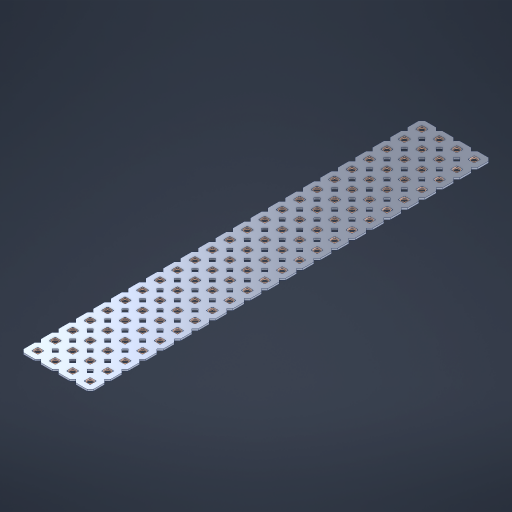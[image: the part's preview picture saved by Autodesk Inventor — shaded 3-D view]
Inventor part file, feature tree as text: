
AUTODESK INVENTOR PART (.ipt)
format: ipt  version: 2023 (Build 270158000, 158)  size: 1,322,496 bytes
history: native  units: in
note: dims shown in document units (in); Inventor stores cm internally (conversion verified against a paired STEP export)
features: other x93, extrude x91, sketch x2, pattern_linear x1
ambient origin geometry x8: Origin, YZ Plane, XZ Plane, XY Plane, X Axis, Y Axis, Z Axis, Center Point
bodies: Solid1 (feature_tree), Body (feature_tree)
feature tree (187):
  pattern_linear  "Rectangular Pattern1"  Spacing1=0.09in  [1 undecoded]
  sketch  "Sketch1"  dims[d1=0.5in]
  sketch  "Sketch2"  dims[d2=0.182in d3=0.09in d4=0.09in d5=0.09in d6=0.09in d7=0.09in d8=0.09in d9=0.09in d10=0.09in d11=0.02in d13=0.0in d14=0.172in d15=0.0625in d16=0.0in d19=0.5in d22=0.5in]
  other  "Srf1"
  other  "Srf126"
  other  "Srf127"
  other  "Srf128"
  other  "Srf129"
  other  "Srf130"
  other  "Srf131"
  other  "Srf250"
  other  "Srf251"
  other  "Srf252"
  other  "Srf253"
  other  "Srf254"
  other  "Srf255"
  other  "Srf256"
  other  "Srf257"
  other  "Srf258"
  other  "Srf259"
  other  "Srf260"
  other  "Srf261"
  other  "Srf262"
  other  "Srf263"
  other  "Srf264"
  other  "Srf268"
  other  "Srf269"
  other  "Srf270"
  other  "Srf271"
  other  "Srf272"
  other  "Srf273"
  other  "Srf274"
  other  "Srf275"
  other  "Srf276"
  other  "Srf277"
  other  "Srf278"
  other  "Srf279"
  other  "Srf280"
  other  "Srf281"
  other  "Srf282"
  other  "Srf283"
  other  "Srf284"
  other  "Srf285"
  other  "Srf286"
  other  "Srf287"
  other  "Srf288"
  other  "Srf289"
  other  "Srf293"
  other  "Srf294"
  other  "Srf295"
  other  "Srf296"
  other  "Srf297"
  other  "Srf298"
  other  "Srf299"
  other  "Srf300"
  other  "Srf301"
  other  "Srf302"
  other  "Srf303"
  other  "Srf304"
  other  "Srf305"
  other  "Srf306"
  other  "Srf307"
  other  "Srf308"
  other  "Srf309"
  other  "Srf310"
  other  "Srf311"
  other  "Srf312"
  other  "Srf313"
  other  "Srf314"
  other  "Srf318"
  other  "Srf319"
  other  "Srf320"
  other  "Srf321"
  other  "Srf322"
  other  "Srf323"
  other  "Srf324"
  other  "Srf325"
  other  "Srf326"
  other  "Srf327"
  other  "Srf328"
  other  "Srf329"
  other  "Srf330"
  other  "Srf331"
  other  "Srf332"
  other  "Srf333"
  other  "Srf334"
  other  "Srf335"
  other  "Srf336"
  other  "Srf337"
  other  "Srf338"
  other  "Srf339"
  other  "Srf368"
  other  "Srf369"
  other  "Srf370"
  other  "Srf371"
  other  "Circle"
  extrude  "ExtrusionSrf126"  Depth=0.09in
  extrude  "ExtrusionSrf127"  Depth=0.09in
  extrude  "ExtrusionSrf128"  Depth=0.09in
  extrude  "ExtrusionSrf129"  Depth=0.09in
  extrude  "ExtrusionSrf130"  Depth=0.09in
  extrude  "ExtrusionSrf131"  Depth=0.09in
  extrude  "ExtrusionSrf250"  Depth=0.09in
  extrude  "ExtrusionSrf251"  Depth=0.02in
  extrude  "ExtrusionSrf252"  TaperAngle=0.0deg  [1 undecoded]
  extrude  "ExtrusionSrf253"  Depth=0.5in
  extrude  "ExtrusionSrf254"  Depth=0.5in TaperAngle=0.0deg
  extrude  "ExtrusionSrf255"  Depth=0.5in
  extrude  "ExtrusionSrf256"  Depth=0.5in
  extrude  "ExtrusionSrf257"  [1 undecoded]
  extrude  "ExtrusionSrf258"  [1 undecoded]
  extrude  "ExtrusionSrf259"  [1 undecoded]
  extrude  "ExtrusionSrf260"  [1 undecoded]
  extrude  "ExtrusionSrf261"  [1 undecoded]
  extrude  "ExtrusionSrf262"  [1 undecoded]
  extrude  "ExtrusionSrf263"  [1 undecoded]
  extrude  "ExtrusionSrf264"  [1 undecoded]
  extrude  "ExtrusionSrf268"  [1 undecoded]
  extrude  "ExtrusionSrf269"  [1 undecoded]
  extrude  "ExtrusionSrf270"  [1 undecoded]
  extrude  "ExtrusionSrf271"  [1 undecoded]
  extrude  "ExtrusionSrf272"  [1 undecoded]
  extrude  "ExtrusionSrf273"  [1 undecoded]
  extrude  "ExtrusionSrf274"  [1 undecoded]
  extrude  "ExtrusionSrf275"  [1 undecoded]
  extrude  "ExtrusionSrf276"  [1 undecoded]
  extrude  "ExtrusionSrf277"  [1 undecoded]
  extrude  "ExtrusionSrf278"  [1 undecoded]
  extrude  "ExtrusionSrf279"  [1 undecoded]
  extrude  "ExtrusionSrf280"  [1 undecoded]
  extrude  "ExtrusionSrf281"  [1 undecoded]
  extrude  "ExtrusionSrf282"  [1 undecoded]
  extrude  "ExtrusionSrf283"  [1 undecoded]
  extrude  "ExtrusionSrf284"  [1 undecoded]
  extrude  "ExtrusionSrf285"  [1 undecoded]
  extrude  "ExtrusionSrf286"  [1 undecoded]
  extrude  "ExtrusionSrf287"  [1 undecoded]
  extrude  "ExtrusionSrf288"  [1 undecoded]
  extrude  "ExtrusionSrf289"  [1 undecoded]
  extrude  "ExtrusionSrf293"  [1 undecoded]
  extrude  "ExtrusionSrf294"  [1 undecoded]
  extrude  "ExtrusionSrf295"  [1 undecoded]
  extrude  "ExtrusionSrf296"  [1 undecoded]
  extrude  "ExtrusionSrf297"  [1 undecoded]
  extrude  "ExtrusionSrf298"  [1 undecoded]
  extrude  "ExtrusionSrf299"  [1 undecoded]
  extrude  "ExtrusionSrf300"  [1 undecoded]
  extrude  "ExtrusionSrf301"  [1 undecoded]
  extrude  "ExtrusionSrf302"  [1 undecoded]
  extrude  "ExtrusionSrf303"  [1 undecoded]
  extrude  "ExtrusionSrf304"  [1 undecoded]
  extrude  "ExtrusionSrf305"  [1 undecoded]
  extrude  "ExtrusionSrf306"  [1 undecoded]
  extrude  "ExtrusionSrf307"  [1 undecoded]
  extrude  "ExtrusionSrf308"  [1 undecoded]
  extrude  "ExtrusionSrf309"  [1 undecoded]
  extrude  "ExtrusionSrf310"  [1 undecoded]
  extrude  "ExtrusionSrf311"  [1 undecoded]
  extrude  "ExtrusionSrf312"  [1 undecoded]
  extrude  "ExtrusionSrf313"  [1 undecoded]
  extrude  "ExtrusionSrf314"  [1 undecoded]
  extrude  "ExtrusionSrf318"  [1 undecoded]
  extrude  "ExtrusionSrf319"  [1 undecoded]
  extrude  "ExtrusionSrf320"  [1 undecoded]
  extrude  "ExtrusionSrf321"  [1 undecoded]
  extrude  "ExtrusionSrf322"  [1 undecoded]
  extrude  "ExtrusionSrf323"  [1 undecoded]
  extrude  "ExtrusionSrf324"  [1 undecoded]
  extrude  "ExtrusionSrf325"  [1 undecoded]
  extrude  "ExtrusionSrf326"  [1 undecoded]
  extrude  "ExtrusionSrf327"  [1 undecoded]
  extrude  "ExtrusionSrf328"  [1 undecoded]
  extrude  "ExtrusionSrf329"  [1 undecoded]
  extrude  "ExtrusionSrf330"  [1 undecoded]
  extrude  "ExtrusionSrf331"  [1 undecoded]
  extrude  "ExtrusionSrf332"  [1 undecoded]
  extrude  "ExtrusionSrf333"  [1 undecoded]
  extrude  "ExtrusionSrf334"  [1 undecoded]
  extrude  "ExtrusionSrf335"  [1 undecoded]
  extrude  "ExtrusionSrf336"  [1 undecoded]
  extrude  "ExtrusionSrf337"  [1 undecoded]
  extrude  "ExtrusionSrf338"  [1 undecoded]
  extrude  "ExtrusionSrf339"  [1 undecoded]
  extrude  "ExtrusionSrf368"  [1 undecoded]
  extrude  "ExtrusionSrf369"  [1 undecoded]
  extrude  "ExtrusionSrf370"  [1 undecoded]
  extrude  "ExtrusionSrf371"  [1 undecoded]
note: 80 required parameter values undecoded (feature->parameter linkage not recoverable at this tier; creation-order binding heuristic only, values carry confidence <= 0.55)
